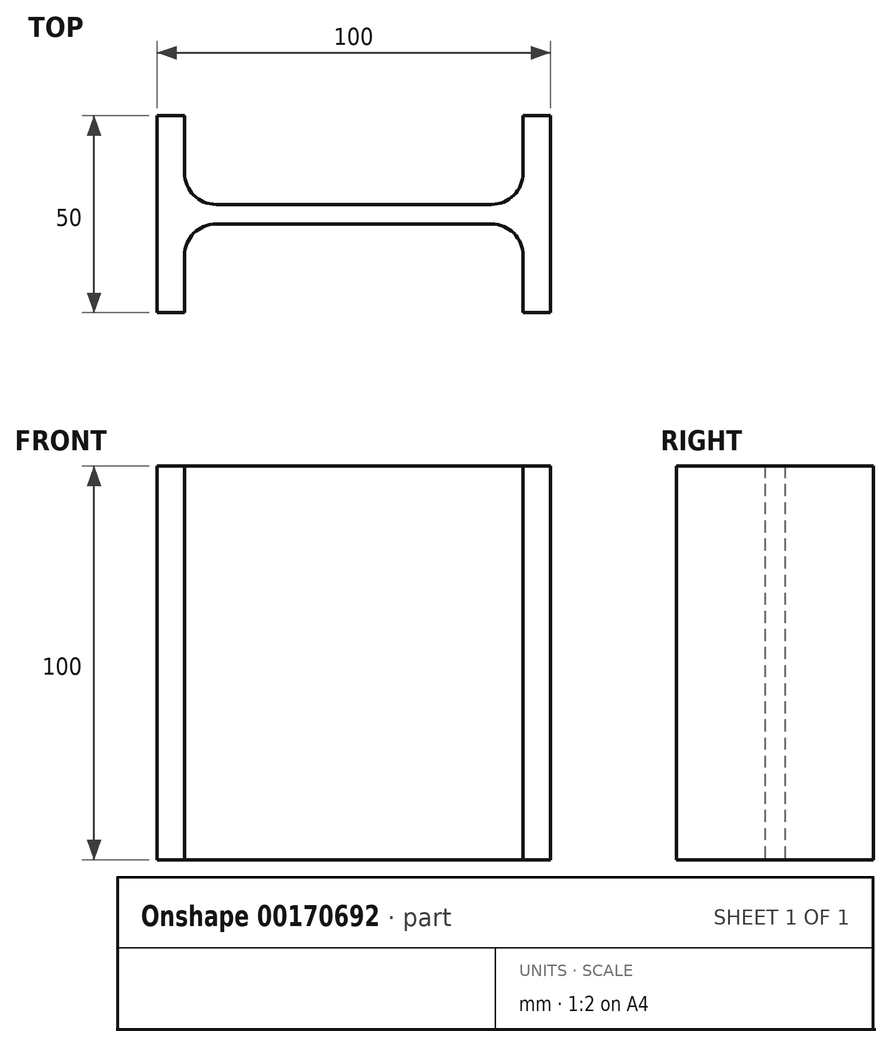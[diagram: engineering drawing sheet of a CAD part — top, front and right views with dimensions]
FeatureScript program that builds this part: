
annotation { "Feature Type Name" : "Feature", "Feature Type Description" : "" }
export const myFeature = defineFeature(function(context is Context, id is Id, definition is map)
    precondition{}
    {
        {
            var Q0;
            Q0=qCreatedBy(makeId("Top.planeOp"),FACE);
            var sketch = newSketch(context, id + "F0", { "sketchPlane" : qUnion([Q0])});
            skLineSegment(sketch, "E0", {"start": v(-50, 25) * mm, "end": v(-50, -25) * mm});
            skLineSegment(sketch, "E1", {"start": v(-50, -25) * mm, "end": v(-43, -25) * mm});
            skLineSegment(sketch, "E2", {"start": v(-43, -25) * mm, "end": v(-43, -2.5) * mm});
            skLineSegment(sketch, "E3", {"start": v(-43, -2.5) * mm, "end": v(43, -2.5) * mm});
            skLineSegment(sketch, "E4", {"start": v(43, -2.5) * mm, "end": v(43, -25) * mm});
            skLineSegment(sketch, "E5", {"start": v(43, -25) * mm, "end": v(50, -25) * mm});
            skLineSegment(sketch, "E6", {"start": v(-50, 25) * mm, "end": v(-43, 25) * mm});
            skLineSegment(sketch, "E7", {"start": v(-43, 25) * mm, "end": v(-43, 2.5) * mm});
            skLineSegment(sketch, "E8", {"start": v(-43, 2.5) * mm, "end": v(43, 2.5) * mm});
            skLineSegment(sketch, "E9", {"start": v(43, 2.5) * mm, "end": v(43, 25) * mm});
            skLineSegment(sketch, "E10", {"start": v(43, 25) * mm, "end": v(50, 25) * mm});
            skLineSegment(sketch, "E11", {"start": v(50, 25) * mm, "end": v(50, -25) * mm});
            skSolve(sketch);
        }
        {
            var Q0;
            Q0 = qSketchRegion(id + "F0", true);
            extrude(context, id + "F1", {"entities" : qUnion([Q0]), "depth" : 100 * mm});
        }
        {
            var Q0;
            Q0=makeQuery(id+"F1.opExtrude","SWEPT_EDGE",EDGE,{"disambiguationData":[OSD([sQuery(id+"F0.wireOp",EDGE,"E3"),sQuery(id+"F0.wireOp",EDGE,"E4")])]});
            var Q1;
            Q1=makeQuery(id+"F1.opExtrude","SWEPT_EDGE",EDGE,{"disambiguationData":[OSD([sQuery(id+"F0.wireOp",EDGE,"E2"),sQuery(id+"F0.wireOp",EDGE,"E3")])]});
            var Q2;
            Q2=makeQuery(id+"F1.opExtrude","SWEPT_EDGE",EDGE,{"disambiguationData":[OSD([sQuery(id+"F0.wireOp",EDGE,"E7"),sQuery(id+"F0.wireOp",EDGE,"E8")])]});
            var Q3;
            Q3=makeQuery(id+"F1.opExtrude","SWEPT_EDGE",EDGE,{"disambiguationData":[OSD([sQuery(id+"F0.wireOp",EDGE,"E8"),sQuery(id+"F0.wireOp",EDGE,"E9")])]});
            fillet(context, id + "F2", {"entities" : qUnion([Q0, Q1, Q2, Q3]), "radius" : 8 * mm, "tangentPropagation" : true, "allowEdgeOverflow" : false});
        }
    });
